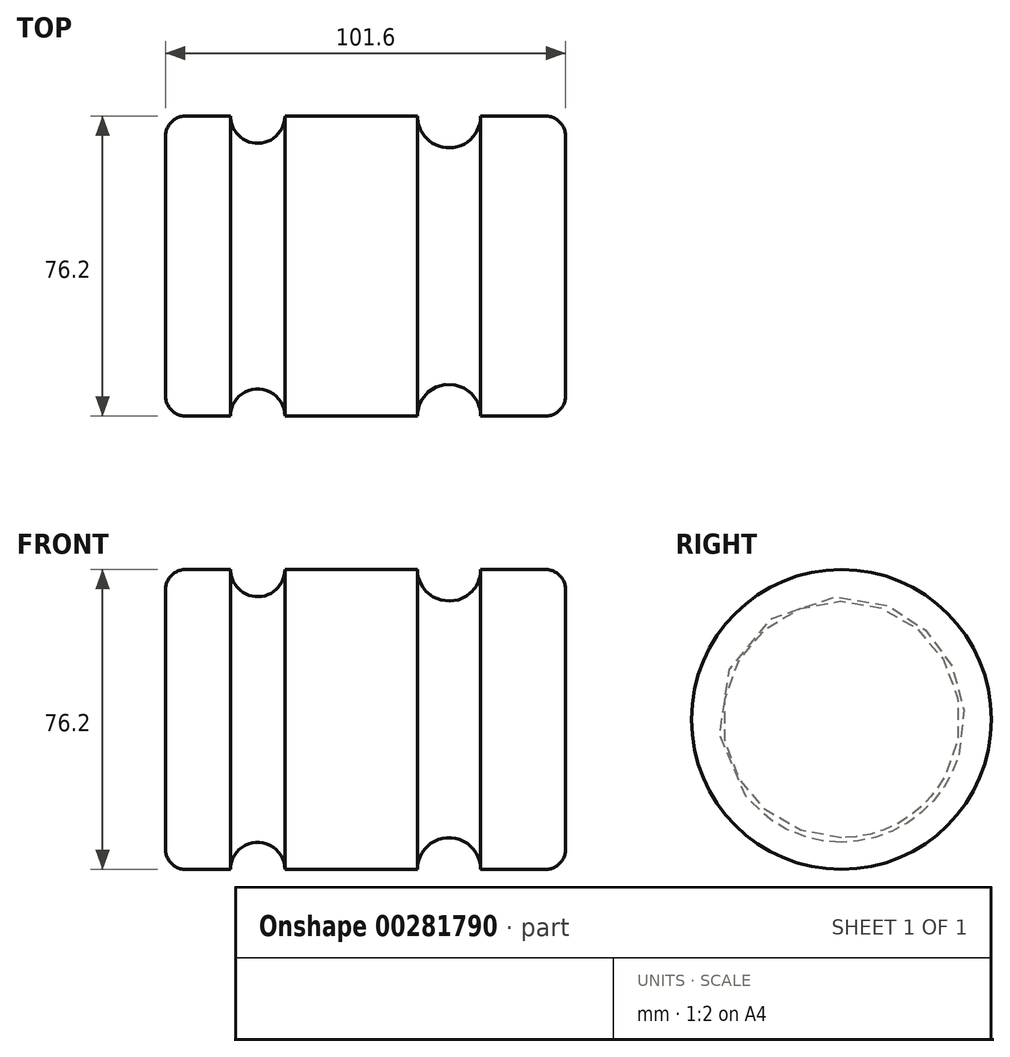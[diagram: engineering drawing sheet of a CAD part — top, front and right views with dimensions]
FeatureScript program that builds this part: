
annotation { "Feature Type Name" : "Feature", "Feature Type Description" : "" }
export const myFeature = defineFeature(function(context is Context, id is Id, definition is map)
    precondition{}
    {
        {
            var Q0;
            Q0=qCreatedBy(makeId("Front.planeOp"),FACE);
            var sketch = newSketch(context, id + "F0", { "sketchPlane" : qUnion([Q0])});
            skLineSegment(sketch, "E0.bottom", {"start": v(74.88, -6.89) * mm, "end": v(53.34, -6.89) * mm});
            skLineSegment(sketch, "E0.top", {"start": v(74.88, -44.99) * mm, "end": v(-26.72, -44.99) * mm});
            skLineSegment(sketch, "E0.left", {"start": v(74.88, -6.89) * mm, "end": v(74.88, -44.99) * mm});
            skLineSegment(sketch, "E0.right", {"start": v(-26.72, -6.89) * mm, "end": v(-26.72, -44.99) * mm});
            skArc(sketch, "E1", {"start": v(-10.23, -6.89) * mm, "mid": v(-3.32, -13.8) * mm, "end": v(3.59, -6.89) * mm});
            skArc(sketch, "E2", {"start": v(37.23, -6.89) * mm, "mid": v(45.29, -14.94) * mm, "end": v(53.34, -6.89) * mm});
            skLineSegment(sketch, "E3.trimOffspring", {"start": v(37.23, -6.89) * mm, "end": v(3.59, -6.89) * mm});
            skLineSegment(sketch, "E4.trimOffspring", {"start": v(-10.23, -6.89) * mm, "end": v(-26.72, -6.89) * mm});
            skSolve(sketch);
        }
        {
            var Q0;
            Q0 = qSketchRegion(id + "F0", true);
            var Q1;
            Q1=sQuery(id+"F0.wireOp",EDGE,"E0.top");
            revolve(context, id + "F1", {"entities" : qUnion([Q0]), "axis" : qUnion([Q1]), "revolveType" : RevolveType.FULL});
        }
        {
            var Q0;
            Q0=makeQuery(id+"F1.opRevolve","SWEPT_EDGE",EDGE,{"disambiguationData":[OSD([sQuery(id+"F0.wireOp",EDGE,"E0.right"),sQuery(id+"F0.wireOp",EDGE,"E4.trimOffspring")])]});
            var Q1;
            Q1=makeQuery(id+"F1.opRevolve","SWEPT_EDGE",EDGE,{"disambiguationData":[OSD([sQuery(id+"F0.wireOp",EDGE,"E0.bottom"),sQuery(id+"F0.wireOp",EDGE,"E0.left")])]});
            fillet(context, id + "F2", {"entities" : qUnion([Q0, Q1]), "radius" : 5.08 * mm, "tangentPropagation" : true, "allowEdgeOverflow" : false});
        }
    });
